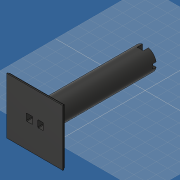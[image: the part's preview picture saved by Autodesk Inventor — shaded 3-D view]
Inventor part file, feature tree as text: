
AUTODESK INVENTOR PART (.ipt)
format: ipt  version: 2019 (Build 230136000, 136)  size: 228,864 bytes
history: native  units: mm
features: extrude x6, sketch x3, hole x1, other x1
ambient origin geometry x8: Origin, YZ Plane, XZ Plane, XY Plane, X Axis, Y Axis, Z Axis, Center Point
bodies: Volumenkörper1 (feature_tree)
feature tree (11):
  sketch  "Skizze1"  dims[d3=194.899mm d4=0.0mm d5=12.5mm]
  extrude  "Extrusion1"  Depth=12.5mm
  extrude  "Extrusion4"  Depth=9.5mm
  extrude  "Extrusion6"  Depth=1.0mm
  extrude  "Extrusion5"  Depth=9.0mm
  sketch  "Skizze2"  dims[d6=11.0mm d7=9.5mm]
  extrude  "Extrusion2"  Depth=17.0mm
  extrude  "Extrusion3"  Depth=13.5mm
  hole  "Bohrung1"  [1 undecoded]
  other  "Spirale1"
  sketch  "Skizze3"  dims[d9=1.0mm d10=1.0mm d12=9.0mm d14=40.0mm d15=13.5mm d16=30.5mm d17=30.0mm d18=9.5mm d19=100.0mm d20=100.0mm d21=1.2mm d22=2.0mm d23=0.0mm d24=2.0mm d25=0.0mm d26=12.0mm d27=0.5mm d28=12.5mm d29=180.0mm d30=160.0mm d31=0.0mm d32=90.0deg d33=90.0deg d34=0.0mm d35=0.0mm d37=40.0mm d40=2.2mm d41=4.0mm d42=4.0mm d43=2.0mm d44=90.0deg d45=5.0mm d46=0.0mm d47=30.0mm d48=90.0deg d49=45.0deg d50=10.5mm d52=10.0mm d53=0.0mm d55=8.0mm d56=6.0mm d57=0.0mm d58=17.0mm d59=0.0mm]
note: 1 required parameter value undecoded (feature->parameter linkage not recoverable at this tier; creation-order binding heuristic only, values carry confidence <= 0.55)
